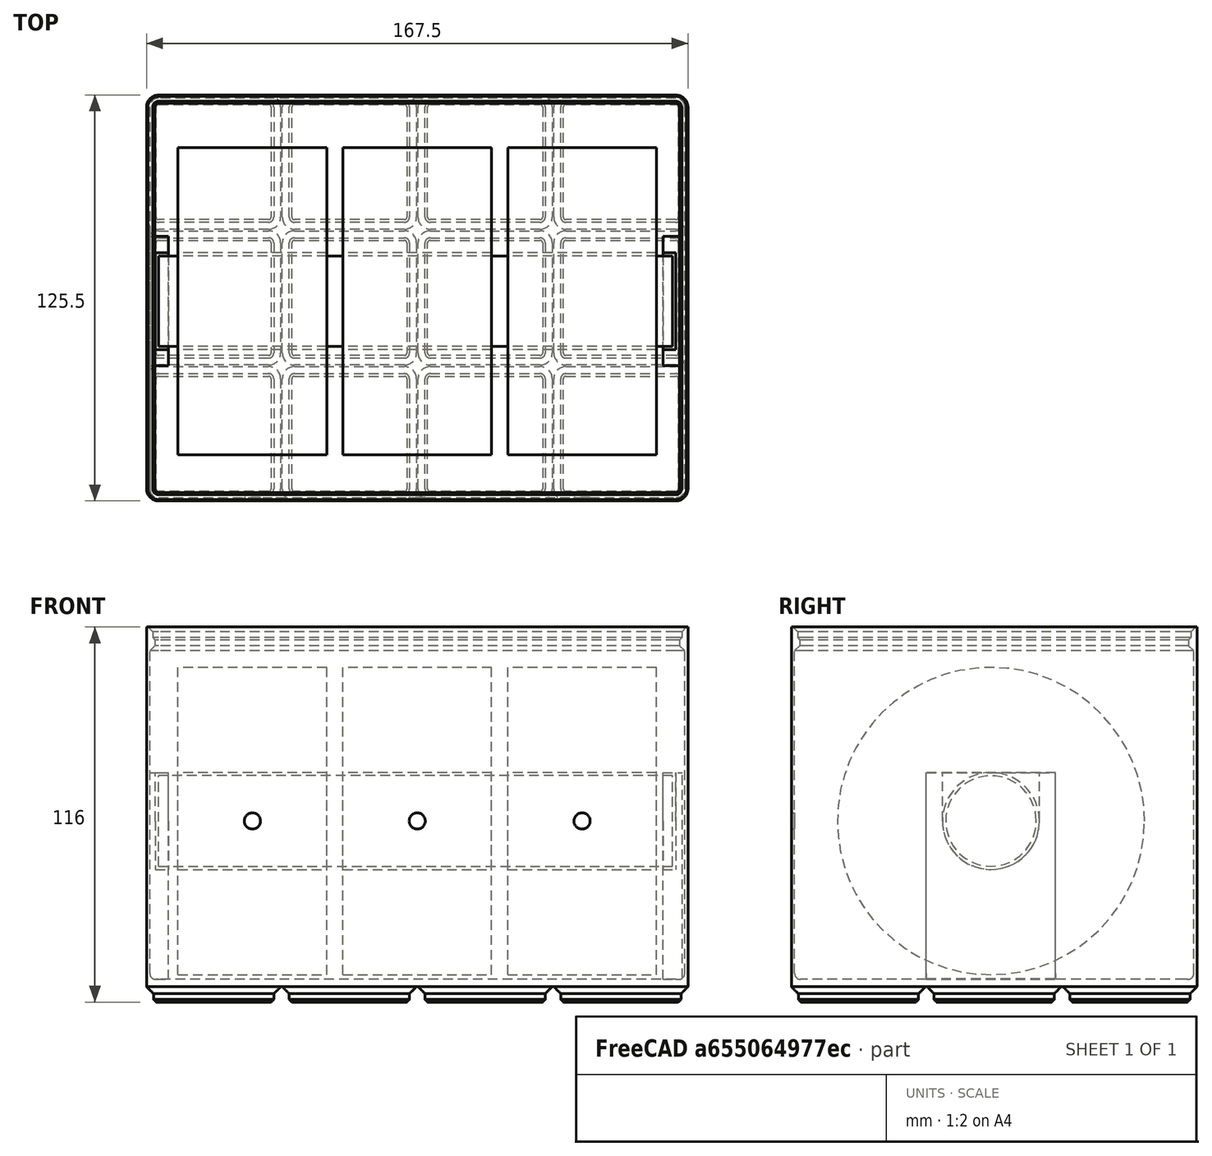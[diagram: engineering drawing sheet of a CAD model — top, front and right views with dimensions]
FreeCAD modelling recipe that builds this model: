
FCSTD DOCUMENT  (FreeCAD 1.0R1.0.1)
Label: LiYv_Store_3spools
License: All rights reserved
LicenseURL: http://en.wikipedia.org/wiki/All_rights_reserved
objects: Part::Cylinder×11, Part::Cut×5, Part::MultiFuse×4, Part::Box×3, Part::FeaturePython×1
note: 24 computed .brp shape members not serialized (recipe doc carries the construction recipe); baked Part::Feature solids carry a one-line shape summary decoded from their .brp

FEATURE [Part::FeaturePython] SimpleStorageBin  # WARN: FeaturePython — macro-defined, semantics opaque (R4)
  BaseProfileBottomChamfer = 0.8
  BaseProfileHeight = 4.75
  BaseProfileTopChamfer = 2.15
  BaseProfileVerticalSection = 1.8
  Baseplate = false
  BinBottomRadius = 0.8
  BinOuterRadius = 3.75
  BinVerticalRadius = 1.6
  Clearance = 0.25
  CustomHeight = 42
  DividerThickness = 1.2
  GenerationLocation = 0
  HeightUnitValue = 7
  HeightUnits = 16
  InsideFilletRadius = 1.85
  LabelShelfAngle = 45
  LabelShelfLength = 42
  LabelShelfPlacement = 0
  LabelShelfStackingOffset = 0.4
  LabelShelfStyle = 0
  LabelShelfVerticalThickness = 1.2
  LabelShelfWidth = 12
  MagnetHoleDepth = 2.4
  MagnetHoleDiameter = 6.2
  MagnetHoleDistanceFromEdge = 8
  MagnetHoles = false
  MagnetHolesShape = 0
  NonStandardHeight = false
  Scoop = false
  ScoopRadius = 21
  ScrewHoleDepth = 6
  ScrewHoleDiameter = 3
  ScrewHoles = false
  SequentialBridgingLayerHeight = 0.2
  StackingLip = true
  StackingLipBottomChamfer = 0.7
  StackingLipTopChamfer = 1.5
  StackingLipTopLedge = 0.4
  StackingLipVerticalSection = 1.8
  TotalHeight = 112
  UsableHeight = 105
  WallThickness = 1
  version = 0.11.9
  xDividerHeight = 0
  xDividers = 0
  xGridSize = 42
  xGridUnits = 4
  xLocationOffset = 0
  xTotalWidth = 167.5
  yDividerHeight = 0
  yDividers = 0
  yGridSize = 42
  yGridUnits = 3
  yLocationOffset = 0
  yTotalWidth = 125.5
  expr: BaseProfileHeight = BaseProfileBottomChamfer + BaseProfileVerticalSection + BaseProfileTopChamfer
  expr: TotalHeight = NonStandardHeight == 1 ? CustomHeight : HeightUnits * HeightUnitValue
  expr: xTotalWidth = xGridUnits * xGridSize - (Baseplate == 1 ? 0 mm : 2 * Clearance)
  expr: yTotalWidth = yGridUnits * yGridSize - (Baseplate == 1 ? 0 mm : 2 * Clearance)
FEATURE [Part::Cylinder] Cylinder
  Angle = 360
  AttacherType = Attacher::AttachEngine3D
  FirstAngle = 0
  Height = 46
  Radius = 47.5
  SecondAngle = 0
FEATURE [Part::Cylinder] Cylinder001
  Angle = 360
  AttacherType = Attacher::AttachEngine3D
  FirstAngle = 0
  Height = 46
  Radius = 15
  SecondAngle = 0
FEATURE [Part::Cut] Cut
  Base = -> Cylinder
  Placement = pos=(5,62,-56) rot=(0,1,0;1.5708rad)
  Tool = -> Cylinder001
FEATURE [Part::Cylinder] Cylinder002
  Angle = 360
  AttacherType = Attacher::AttachEngine3D
  FirstAngle = 0
  Height = 46
  Radius = 47.5
  SecondAngle = 0
FEATURE [Part::Cylinder] Cylinder003
  Angle = 360
  AttacherType = Attacher::AttachEngine3D
  FirstAngle = 0
  Height = 46
  Radius = 15
  SecondAngle = 0
FEATURE [Part::Cut] Cut001
  Base = -> Cylinder002
  Placement = pos=(56,62,-56) rot=(0,1,0;1.5708rad)
  Tool = -> Cylinder003
FEATURE [Part::Cylinder] Cylinder004
  Angle = 360
  AttacherType = Attacher::AttachEngine3D
  FirstAngle = 0
  Height = 46
  Radius = 47.5
  SecondAngle = 0
FEATURE [Part::Cylinder] Cylinder005
  Angle = 360
  AttacherType = Attacher::AttachEngine3D
  FirstAngle = 0
  Height = 46
  Radius = 15
  SecondAngle = 0
FEATURE [Part::Cut] Cut002
  Base = -> Cylinder004
  Placement = pos=(107,62,-56) rot=(0,1,0;1.5708rad)
  Tool = -> Cylinder005
FEATURE [Part::MultiFuse] Fusion  label="Spulen"
  Placement = pos=(5,0,0) rot=(0,0,1;0rad)
  Shapes = -> [Cut002,Cut,Cut001]
FEATURE [Part::Cylinder] Cylinder006  label="Achse"
  Angle = 360
  AttacherType = Attacher::AttachEngine3D
  FirstAngle = 0
  Height = 159
  Placement = pos=(4,62,-56) rot=(0,1,0;1.5708rad)
  Radius = 14
  SecondAngle = 0
FEATURE [Part::Box] Box  label="Cube"
  AttacherType = Attacher::AttachEngine3D
  Height = 64
  Length = 6
  Placement = pos=(1,42,-105) rot=(0,0,1;0rad)
  Width = 40
FEATURE [Part::Box] Box001  label="Cube001"
  AttacherType = Attacher::AttachEngine3D
  Height = 64
  Length = 6
  Placement = pos=(160,42,-105) rot=(0,0,1;0rad)
  Width = 40
FEATURE [Part::Cylinder] Cylinder007
  Angle = 360
  AttacherType = Attacher::AttachEngine3D
  FirstAngle = 0
  Height = 161
  Placement = pos=(3,62,-56) rot=(0,1,0;1.5708rad)
  Radius = 15
  SecondAngle = 0
FEATURE [Part::Box] Box002  label="Cube002"
  AttacherType = Attacher::AttachEngine3D
  Height = 15
  Length = 161
  Placement = pos=(3,47,-56) rot=(0,0,1;0rad)
  Width = 30
FEATURE [Part::MultiFuse] Fusion001
  Shapes = -> [Cylinder007,Box002]
FEATURE [Part::MultiFuse] Fusion002
  Shapes = -> [Box,Box001,SimpleStorageBin]
FEATURE [Part::Cylinder] Cylinder008
  Angle = 360
  AttacherType = Attacher::AttachEngine3D
  FirstAngle = 0
  Height = 10
  Placement = pos=(33,0,-56) rot=(1,0,0;1.5708rad)
  Radius = 2.5
  SecondAngle = 0
FEATURE [Part::Cylinder] Cylinder009
  Angle = 360
  AttacherType = Attacher::AttachEngine3D
  FirstAngle = 0
  Height = 10
  Placement = pos=(84,0,-56) rot=(1,0,0;1.5708rad)
  Radius = 2.5
  SecondAngle = 0
FEATURE [Part::Cylinder] Cylinder010
  Angle = 360
  AttacherType = Attacher::AttachEngine3D
  FirstAngle = 0
  Height = 10
  Placement = pos=(135,0,-56) rot=(1,0,0;1.5708rad)
  Radius = 2.5
  SecondAngle = 0
FEATURE [Part::MultiFuse] Fusion003
  Placement = pos=(0,7,0) rot=(0,0,1;0rad)
  Shapes = -> [Cylinder008,Cylinder009,Cylinder010]
FEATURE [Part::Cut] Cut003
  Base = -> Fusion002
  Tool = -> Fusion001
FEATURE [Part::Cut] Cut004  label="Box"
  Base = -> Cut003
  Tool = -> Fusion003
